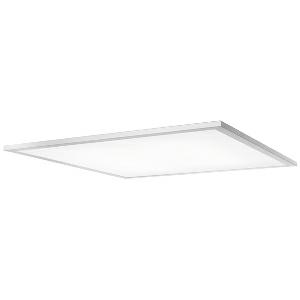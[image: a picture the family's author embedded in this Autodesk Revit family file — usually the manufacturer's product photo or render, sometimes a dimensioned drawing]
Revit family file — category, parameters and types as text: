
# Revit family: dotoo_fit_-_dfe_4000_840_d_sm625_00808114_6fff
name_source: partatom
category: Lighting Fixtures
units: mm (PartAtom-declared; Revit-internal decimal feet)

## family parameters
Cut with Voids When Loaded = No
Host = Face
Light Source = No
Part Type = Normal
Room Calculation Point = No
Round Connector Dimension = Use Diameter
Shared = No

## types (1)
- DOTOO.fit - DFE 4000/840/D SM625 (1 x LED, 4100 lm, 4000K)
    Apparent Load = 30 VA
    Approval mark = CE
    CIE Flux Codes = 66 90 98 100 100
    Color Rendering = 80-89
    Color Temperature = 4000K
    Control Gear = Electronic ballast
    Default Elevation = 1800 mm
    Description = DFE 4000/840/D|Recessed modular luminaire|light source:  |work equipment: Electronic ballast|connected load: 220-240V, 50/60Hz|Power consumption: approx. 30 W|standby: approx. 0,50|power factor: approx. 0,900|luminous flux: 4100 lm|luminous efficacy: 136 lm/W|light distribution: Direct|direct ratio: approx. 100 %|colour temperature: Cold white, ca. 4000 K|color rendering index (CRI): >= 80|chromaticity tolerance:  3 SDCM|System of protection: IP 20|class of protection: II|technology: Continuously dimmable|operation: External|luminaire body|material: Sectional aluminium|colour: White|weight (net): approx. 3.1 kg|mains lead: 0.50 m Connector|glare control: Prism aperture|luminance(L65): <= 2700 cd/m|unified glare rating(4H 8H): <=  19|special features: DALI Load 1x, TouchDIM - dimming via standard switch, Direct light component with edge light and light-guide technology for homogenous light exit, Flicker-free, System dimension 625 x 625 mm, Strain relief with the possibility of through-wiring|
    Height = 0 mm  [stored 0 ft]
    Lamp = 1 x LED
    Lamp Light Flux = 4100 lm
    Lamp count = 1
    Length = 622 mm
    Luminous efficacy = 137 lm/W
    Manufacturer = Waldmann
    ModVariant = No
    Model = 00808114
    Mounting Place = Ceiling
    Mounting Type = Recessed
    Number of Poles = 1
    OnlyDefault = Yes
    Power Factor = 1
    Product Name = DOTOO.fit - DFE 4000/840/D SM625
    Product group = Recessed luminaire
    ProductGroupID = 4
    Protection Class = Protection class II
    Protection Degree = IP 20
    RLX_Detail_Level = 1
    RLX_Emergency_Light_Flux = 0 lm
    RLX_Emergency_Type = 0
    RLX_Emergency_Type_DB = No
    RlxData = <blob elided: 37753 chars, md5=4ee22e52>
    Socket = socket
    Standby Power = 0 W
    System Light Flux = 4100 lm
    System Power = 30 W
    Type Comments = Product without accessories
    Type Image = 113328000-00692486.jpg
    URL = http://relux.com
    VarID = ---
    Voltage = 230 V
    Voltage Range = 220-240 V
    Weight = 0.00 kg
    Width = 622 mm

note: [stored X ft] marks values corroborated as IEEE doubles in the binary element streams (Revit-internal decimal feet)

## geometry (parser evidence)
native form markers: Blend x4, Sweep x9
no freeform markers — native parametric forms only
